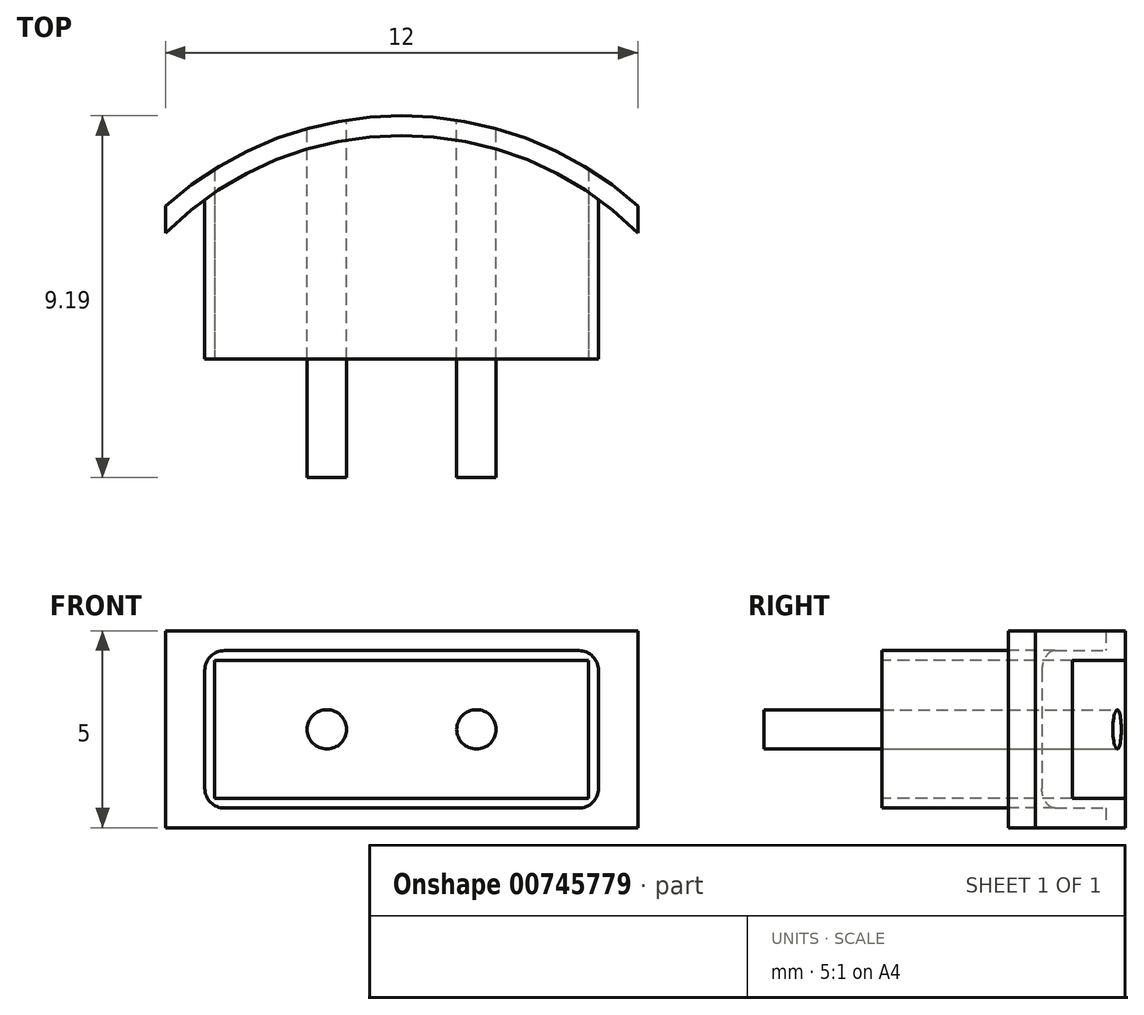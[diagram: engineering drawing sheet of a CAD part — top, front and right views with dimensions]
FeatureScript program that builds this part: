
annotation { "Feature Type Name" : "Feature", "Feature Type Description" : "" }
export const myFeature = defineFeature(function(context is Context, id is Id, definition is map)
    precondition{}
    {
        {
            var Q0;
            Q0=qCreatedBy(makeId("Top.planeOp"),FACE);
            var sketch = newSketch(context, id + "F0", { "sketchPlane" : qUnion([Q0])});
            skArc(sketch, "E0", {"start": v(6, 6.7) * mm, "mid": v(0, 9) * mm, "end": v(-6, 6.7) * mm});
            skArc(sketch, "E1", {"start": v(6, 6.02) * mm, "mid": v(0, 8.5) * mm, "end": v(-6, 6.02) * mm});
            skLineSegment(sketch, "E2", {"start": v(-6, 6.02) * mm, "end": v(-6, 6.7) * mm});
            skLineSegment(sketch, "E3", {"start": v(6, 6.02) * mm, "end": v(6, 6.7) * mm});
            skSolve(sketch);
        }
        {
            var Q0;
            Q0 = qSketchRegion(id + "F0", true);
            extrude(context, id + "F1", {"entities" : qUnion([Q0]), "depth" : 5 * mm, "offsetDistance" : 25 * mm});
        }
        {
            var Q0;
            Q0=qCreatedBy(makeId("Front.planeOp"),FACE);
            var sketch = newSketch(context, id + "F2", { "sketchPlane" : qUnion([Q0])});
            skLineSegment(sketch, "E4.bottom", {"start": v(-5, 0.5) * mm, "end": v(5, 0.5) * mm});
            skLineSegment(sketch, "E4.top", {"start": v(-5, 4.5) * mm, "end": v(5, 4.5) * mm});
            skLineSegment(sketch, "E4.left", {"start": v(-5, 0.5) * mm, "end": v(-5, 4.5) * mm});
            skLineSegment(sketch, "E4.right", {"start": v(5, 0.5) * mm, "end": v(5, 4.5) * mm});
            skSolve(sketch);
        }
        {
            var Q0;
            Q0 = qSketchRegion(id + "F2", true);
            extrude(context, id + "F3", {"entities" : qUnion([Q0]), "operationType" : NewBodyOperationType.REMOVE, "oppositeDirection" : true, "depth" : 25 * mm, "offsetDistance" : 25 * mm});
        }
        {
            var Q0;
            Q0=makeQuery(id+"F3.boolean.opBoolean","COPY",EDGE,{"derivedFrom":makeQuery(id+"F3.opExtrude","SWEPT_EDGE",EDGE,{"disambiguationData":[OSD([sQuery(id+"F2.wireOp",EDGE,"E4.top"),sQuery(id+"F2.wireOp",EDGE,"E4.right")])]})});
            var Q1;
            Q1=makeQuery(id+"F3.boolean.opBoolean","COPY",EDGE,{"derivedFrom":makeQuery(id+"F3.opExtrude","SWEPT_EDGE",EDGE,{"disambiguationData":[OSD([sQuery(id+"F2.wireOp",EDGE,"E4.bottom"),sQuery(id+"F2.wireOp",EDGE,"E4.right")])]})});
            var Q2;
            Q2=makeQuery(id+"F3.boolean.opBoolean","COPY",EDGE,{"derivedFrom":makeQuery(id+"F3.opExtrude","SWEPT_EDGE",EDGE,{"disambiguationData":[OSD([sQuery(id+"F2.wireOp",EDGE,"E4.bottom"),sQuery(id+"F2.wireOp",EDGE,"E4.left")])]})});
            var Q3;
            Q3=makeQuery(id+"F3.boolean.opBoolean","COPY",EDGE,{"derivedFrom":makeQuery(id+"F3.opExtrude","SWEPT_EDGE",EDGE,{"disambiguationData":[OSD([sQuery(id+"F2.wireOp",EDGE,"E4.top"),sQuery(id+"F2.wireOp",EDGE,"E4.left")])]})});
            fillet(context, id + "F4", {"entities" : qUnion([Q0, Q1, Q2, Q3]), "radius" : 0.5 * mm, "tangentPropagation" : true, "allowEdgeOverflow" : false});
        }
        {
            var Q0;
            Q0=qCreatedBy(makeId("Front.planeOp"),FACE);
            var sketch = newSketch(context, id + "F5", { "sketchPlane" : qUnion([Q0])});
            skLineSegment(sketch, "E5.bottom", {"start": v(-4.5, 4.5) * mm, "end": v(4.5, 4.5) * mm});
            skLineSegment(sketch, "E5.top", {"start": v(-4.5, 0.5) * mm, "end": v(4.5, 0.5) * mm});
            skLineSegment(sketch, "E5.left", {"start": v(-5, 4) * mm, "end": v(-5, 1) * mm});
            skLineSegment(sketch, "E5.right", {"start": v(5, 4) * mm, "end": v(5, 1) * mm});
            skPoint(sketch, "E6.visualSharp", {"position": v(-5, 4.5) * mm});
            skArc(sketch, "E6.filletArc", {"start": v(-4.5, 4.5) * mm, "mid": v(-4.85, 4.35) * mm, "end": v(-5, 4) * mm});
            skPoint(sketch, "E7.visualSharp", {"position": v(5, 4.5) * mm});
            skArc(sketch, "E7.filletArc", {"start": v(5, 4) * mm, "mid": v(4.85, 4.35) * mm, "end": v(4.5, 4.5) * mm});
            skPoint(sketch, "E8.visualSharp", {"position": v(5, 0.5) * mm});
            skArc(sketch, "E8.filletArc", {"start": v(4.5, 0.5) * mm, "mid": v(4.85, 0.65) * mm, "end": v(5, 1) * mm});
            skPoint(sketch, "E9.visualSharp", {"position": v(-5, 0.5) * mm});
            skArc(sketch, "E9.filletArc", {"start": v(-5, 1) * mm, "mid": v(-4.85, 0.65) * mm, "end": v(-4.5, 0.5) * mm});
            skSolve(sketch);
        }
        {
            var Q0;
            Q0=makeQuery(id+"F5.imprint","IMPRINT",FACE,{"disambiguationData":[TD([[makeQuery(id+"F5.imprint","IMPRINT",EDGE,{"derivedFrom":sQuery(id+"F5.wireOp",EDGE,"E5.bottom")}),-1.0]])]});
            extrude(context, id + "F6", {"entities" : qUnion([Q0]), "operationType" : NewBodyOperationType.ADD, "oppositeDirection" : true, "depth" : 10 * mm, "offsetDistance" : 25 * mm});
        }
        {
            var Q0;
            Q0=makeQuery(id+"F6.opExtrude","CAP_FACE",FACE,{"disambiguationData":[OSD([sQuery(id+"F5.wireOp",EDGE,"E5.bottom"),sQuery(id+"F5.wireOp",EDGE,"E5.top"),sQuery(id+"F5.wireOp",EDGE,"E5.left"),sQuery(id+"F5.wireOp",EDGE,"E5.right"),sQuery(id+"F5.wireOp",EDGE,"E6.filletArc"),sQuery(id+"F5.wireOp",EDGE,"E7.filletArc"),sQuery(id+"F5.wireOp",EDGE,"E8.filletArc"),sQuery(id+"F5.wireOp",EDGE,"E9.filletArc")])],"isStart":true});
            var sketch = newSketch(context, id + "F7", { "sketchPlane" : qUnion([Q0])});
            skLineSegment(sketch, "E10.bottom", {"start": v(-4.75, 4.25) * mm, "end": v(4.75, 4.25) * mm});
            skLineSegment(sketch, "E10.top", {"start": v(-4.75, 0.75) * mm, "end": v(4.75, 0.75) * mm});
            skLineSegment(sketch, "E10.left", {"start": v(-4.75, 4.25) * mm, "end": v(-4.75, 0.75) * mm});
            skLineSegment(sketch, "E10.right", {"start": v(4.75, 4.25) * mm, "end": v(4.75, 0.75) * mm});
            skSolve(sketch);
        }
        {
            var Q0;
            Q0 = qSketchRegion(id + "F7", true);
            extrude(context, id + "F8", {"entities" : qUnion([Q0]), "operationType" : NewBodyOperationType.REMOVE, "oppositeDirection" : true, "depth" : 50 * mm, "offsetDistance" : 25 * mm});
        }
        {
            var Q0;
            {var subQ2=sQuery(id+"F5.wireOp",EDGE,"E5.bottom");Q0=makeQuery(id+"F6.boolean.opBoolean","SPLIT",FACE,{"disambiguationData":[TD([makeQuery(id+"F1.opExtrude","SWEPT_FACE",FACE,{"disambiguationData":[OSD([sQuery(id+"F0.wireOp",EDGE,"E1")])]})])],"derivedFrom":makeQuery(id+"F6.opExtrude","SWEPT_FACE",FACE,{"disambiguationData":[OSD([subQ2])]})});}
            var sketch = newSketch(context, id + "F9", { "sketchPlane" : qUnion([Q0])});
            skLineSegment(sketch, "E11.bottom", {"start": v(-6.63, 2.81) * mm, "end": v(7.2, 2.81) * mm});
            skLineSegment(sketch, "E11.top", {"start": v(-6.63, -1.56) * mm, "end": v(7.2, -1.56) * mm});
            skLineSegment(sketch, "E11.left", {"start": v(-6.63, 2.81) * mm, "end": v(-6.63, -1.56) * mm});
            skLineSegment(sketch, "E11.right", {"start": v(7.2, 2.81) * mm, "end": v(7.2, -1.56) * mm});
            skSolve(sketch);
        }
        {
            var Q0;
            Q0 = qSketchRegion(id + "F9", true);
            extrude(context, id + "F10", {"entities" : qUnion([Q0]), "operationType" : NewBodyOperationType.REMOVE, "oppositeDirection" : true, "depth" : 25 * mm, "offsetDistance" : 25 * mm});
        }
        {
            var Q0;
            Q0=makeQuery(id+"F10.boolean.opBoolean","COPY",FACE,{"derivedFrom":makeQuery(id+"F10.opExtrude","SWEPT_FACE",FACE,{"disambiguationData":[OSD([sQuery(id+"F9.wireOp",EDGE,"E11.bottom")])]})});
            var sketch = newSketch(context, id + "F11", { "sketchPlane" : qUnion([Q0])});
            skLineSegment(sketch, "E12.bottom", {"start": v(-4.75, 0.75) * mm, "end": v(4.75, 0.75) * mm});
            skLineSegment(sketch, "E12.top", {"start": v(-4.75, 4.25) * mm, "end": v(4.75, 4.25) * mm});
            skLineSegment(sketch, "E12.left", {"start": v(-4.75, 0.75) * mm, "end": v(-4.75, 4.25) * mm});
            skLineSegment(sketch, "E12.right", {"start": v(4.75, 0.75) * mm, "end": v(4.75, 4.25) * mm});
            skSolve(sketch);
        }
        {
            var Q0;
            Q0 = qSketchRegion(id + "F11", true);
            extrude(context, id + "F12", {"entities" : qUnion([Q0]), "oppositeDirection" : true, "depth" : 8 * mm, "offsetDistance" : 25 * mm});
        }
        {
            var Q0;
            Q0=makeQuery(id+"F12.opExtrude","CAP_FACE",FACE,{"disambiguationData":[OSD([sQuery(id+"F11.wireOp",EDGE,"E12.bottom"),sQuery(id+"F11.wireOp",EDGE,"E12.top"),sQuery(id+"F11.wireOp",EDGE,"E12.left"),sQuery(id+"F11.wireOp",EDGE,"E12.right")])],"isStart":true});
            var sketch = newSketch(context, id + "F13", { "sketchPlane" : qUnion([Q0])});
            skCircle(sketch, "E13", {"center": v(-1.9, 2.5) * mm, "radius": 0.5 * mm});
            skPoint(sketch, "E13.centerSnap0", {"position": v(4.75, 2.5) * mm});
            skCircle(sketch, "E14", {"center": v(1.9, 2.5) * mm, "radius": 0.5 * mm});
            skSolve(sketch);
        }
        {
            var Q0;
            Q0 = qSketchRegion(id + "F13", true);
            extrude(context, id + "F14", {"entities" : qUnion([Q0]), "depth" : 3 * mm, "offsetDistance" : 25 * mm, "hasSecondDirection" : true, "secondDirectionOppositeDirection" : true, "secondDirectionDepth" : 7.95 * mm});
        }
        {
            var Q0;
            Q0=qCreatedBy(makeId("Top.planeOp"),FACE);
            var sketch = newSketch(context, id + "F15", { "sketchPlane" : qUnion([Q0])});
            skArc(sketch, "E15", {"start": v(6, 6.7) * mm, "mid": v(0, 9) * mm, "end": v(-6, 6.7) * mm});
            skLineSegment(sketch, "E16", {"start": v(-6, 6.7) * mm, "end": v(-6, 11.83) * mm});
            skLineSegment(sketch, "E17", {"start": v(6, 6.7) * mm, "end": v(6, 11.83) * mm});
            skLineSegment(sketch, "E18", {"start": v(-6, 11.83) * mm, "end": v(6, 11.83) * mm});
            skSolve(sketch);
        }
        {
            var Q0;
            Q0 = qSketchRegion(id + "F15", true);
            extrude(context, id + "F16", {"entities" : qUnion([Q0]), "operationType" : NewBodyOperationType.REMOVE, "depth" : 25 * mm, "offsetDistance" : 25 * mm});
        }
    });
